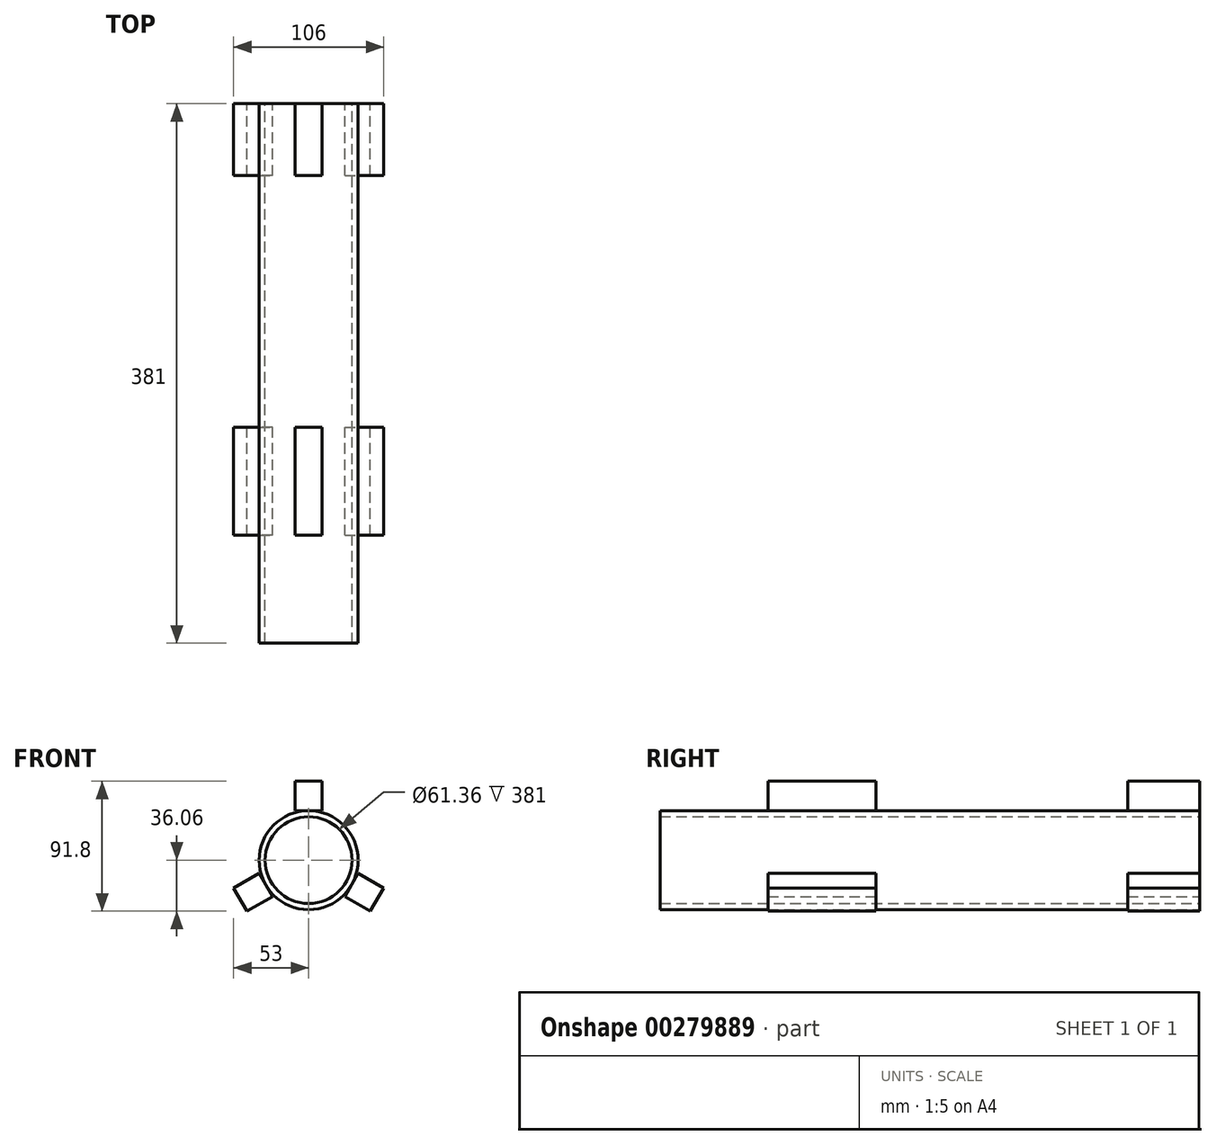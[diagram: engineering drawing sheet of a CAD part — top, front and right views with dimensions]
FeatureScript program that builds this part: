
annotation { "Feature Type Name" : "Feature", "Feature Type Description" : "" }
export const myFeature = defineFeature(function(context is Context, id is Id, definition is map)
    precondition{}
    {
        {
            var Q0;
            Q0=qCreatedBy(makeId("Front.planeOp"),FACE);
            var sketch = newSketch(context, id + "F0", { "sketchPlane" : qUnion([Q0])});
            skCircle(sketch, "E0", {"center": v(0, 0) * mm, "radius": 34.93 * mm});
            skCircle(sketch, "E1", {"center": v(0, 0) * mm, "radius": 30.68 * mm});
            skLineSegment(sketch, "E2.bottom", {"start": v(0, 34.93) * mm, "end": v(9.46, 34.93) * mm});
            skLineSegment(sketch, "E2.top", {"start": v(0, 55.74) * mm, "end": v(9.46, 55.74) * mm});
            skLineSegment(sketch, "E2.right", {"start": v(9.46, 34.93) * mm, "end": v(9.46, 55.74) * mm});
            skLineSegment(sketch, "E3.MirrorCS", {"start": v(0, 55.74) * mm, "end": v(-9.46, 55.74) * mm});
            skLineSegment(sketch, "E4.MirrorCS", {"start": v(0, 34.93) * mm, "end": v(-9.46, 34.93) * mm});
            skLineSegment(sketch, "E5.MirrorCS", {"start": v(-9.46, 34.93) * mm, "end": v(-9.46, 55.74) * mm});
            skLineSegment(sketch, "E6.1.0", {"start": v(-25.52, -25.65) * mm, "end": v(-43.54, -36.06) * mm});
            skLineSegment(sketch, "E6.1.1", {"start": v(-48.27, -27.87) * mm, "end": v(-43.54, -36.06) * mm});
            skLineSegment(sketch, "E6.1.2", {"start": v(-30.25, -17.46) * mm, "end": v(-25.52, -25.65) * mm});
            skLineSegment(sketch, "E6.1.3", {"start": v(-48.27, -27.87) * mm, "end": v(-53, -19.68) * mm});
            skLineSegment(sketch, "E6.1.4", {"start": v(-34.98, -9.27) * mm, "end": v(-53, -19.68) * mm});
            skLineSegment(sketch, "E6.1.5", {"start": v(-30.25, -17.46) * mm, "end": v(-34.98, -9.27) * mm});
            skLineSegment(sketch, "E6.2.0", {"start": v(34.98, -9.27) * mm, "end": v(53, -19.68) * mm});
            skLineSegment(sketch, "E6.2.1", {"start": v(48.27, -27.87) * mm, "end": v(53, -19.68) * mm});
            skLineSegment(sketch, "E6.2.2", {"start": v(30.25, -17.46) * mm, "end": v(34.98, -9.27) * mm});
            skLineSegment(sketch, "E6.2.3", {"start": v(48.27, -27.87) * mm, "end": v(43.54, -36.06) * mm});
            skLineSegment(sketch, "E6.2.4", {"start": v(25.52, -25.65) * mm, "end": v(43.54, -36.06) * mm});
            skLineSegment(sketch, "E6.2.5", {"start": v(30.25, -17.46) * mm, "end": v(25.52, -25.65) * mm});
            skSolve(sketch);
        }
        {
            var Q0;
            Q0=makeQuery(id+"F0.imprint","IMPRINT",FACE,{"disambiguationData":[TD([[makeQuery(id+"F0.imprint","IMPRINT",EDGE,{"derivedFrom":sQuery(id+"F0.wireOp",EDGE,"E1")}),-1.0]])]});
            var Q1;
            Q1=sQuery(id+"F0.wireOp",EDGE,"E0");
            var Q2;
            Q2=sQuery(id+"F0.wireOp",EDGE,"E1");
            extrude(context, id + "F1", {"entities" : qUnion([Q0]), "surfaceEntities" : qUnion([Q1, Q2]), "depth" : 381 * mm});
        }
        {
            var Q0;
            Q0=makeQuery(id+"F0.imprint","IMPRINT",FACE,{"disambiguationData":[TD([[makeQuery(id+"F0.imprint","IMPRINT",EDGE,{"derivedFrom":sQuery(id+"F0.wireOp",EDGE,"E2.bottom")}),1.0]])]});
            var Q1;
            Q1=makeQuery(id+"F0.imprint","IMPRINT",FACE,{"disambiguationData":[TD([[makeQuery(id+"F0.imprint","IMPRINT",EDGE,{"derivedFrom":sQuery(id+"F0.wireOp",EDGE,"E6.2.0")}),-1.0]])]});
            var Q2;
            Q2=makeQuery(id+"F0.imprint","IMPRINT",FACE,{"disambiguationData":[TD([[makeQuery(id+"F0.imprint","IMPRINT",EDGE,{"derivedFrom":sQuery(id+"F0.wireOp",EDGE,"E6.1.0")}),-1.0]])]});
            extrude(context, id + "F2", {"entities" : qUnion([Q0, Q1, Q2]), "depth" : 50.8 * mm});
        }
        {
            var Q0;
            Q0=makeQuery(id+"F2.opExtrude","CAP_FACE",FACE,{"disambiguationData":[OSD([sQuery(id+"F0.wireOp",EDGE,"E2.bottom"),sQuery(id+"F0.wireOp",EDGE,"E2.top"),sQuery(id+"F0.wireOp",EDGE,"E2.right"),sQuery(id+"F0.wireOp",EDGE,"E3.MirrorCS"),sQuery(id+"F0.wireOp",EDGE,"E4.MirrorCS"),sQuery(id+"F0.wireOp",EDGE,"E5.MirrorCS")])],"isStart":false});
            var Q1;
            Q1=makeQuery(id+"F2.opExtrude","CAP_FACE",FACE,{"disambiguationData":[OSD([sQuery(id+"F0.wireOp",EDGE,"E6.1.0"),sQuery(id+"F0.wireOp",EDGE,"E6.1.1"),sQuery(id+"F0.wireOp",EDGE,"E6.1.2"),sQuery(id+"F0.wireOp",EDGE,"E6.1.3"),sQuery(id+"F0.wireOp",EDGE,"E6.1.4"),sQuery(id+"F0.wireOp",EDGE,"E6.1.5")])],"isStart":false});
            var Q2;
            Q2=makeQuery(id+"F2.opExtrude","CAP_FACE",FACE,{"disambiguationData":[OSD([sQuery(id+"F0.wireOp",EDGE,"E6.2.0"),sQuery(id+"F0.wireOp",EDGE,"E6.2.1"),sQuery(id+"F0.wireOp",EDGE,"E6.2.2"),sQuery(id+"F0.wireOp",EDGE,"E6.2.3"),sQuery(id+"F0.wireOp",EDGE,"E6.2.4"),sQuery(id+"F0.wireOp",EDGE,"E6.2.5")])],"isStart":false});
            extrude(context, id + "F3", {"entities" : qUnion([Q0, Q1, Q2]), "depth" : 254 * mm, "hasSecondDirection" : true, "secondDirectionOppositeDirection" : false, "secondDirectionDepth" : 177.8 * mm});
        }
    });
